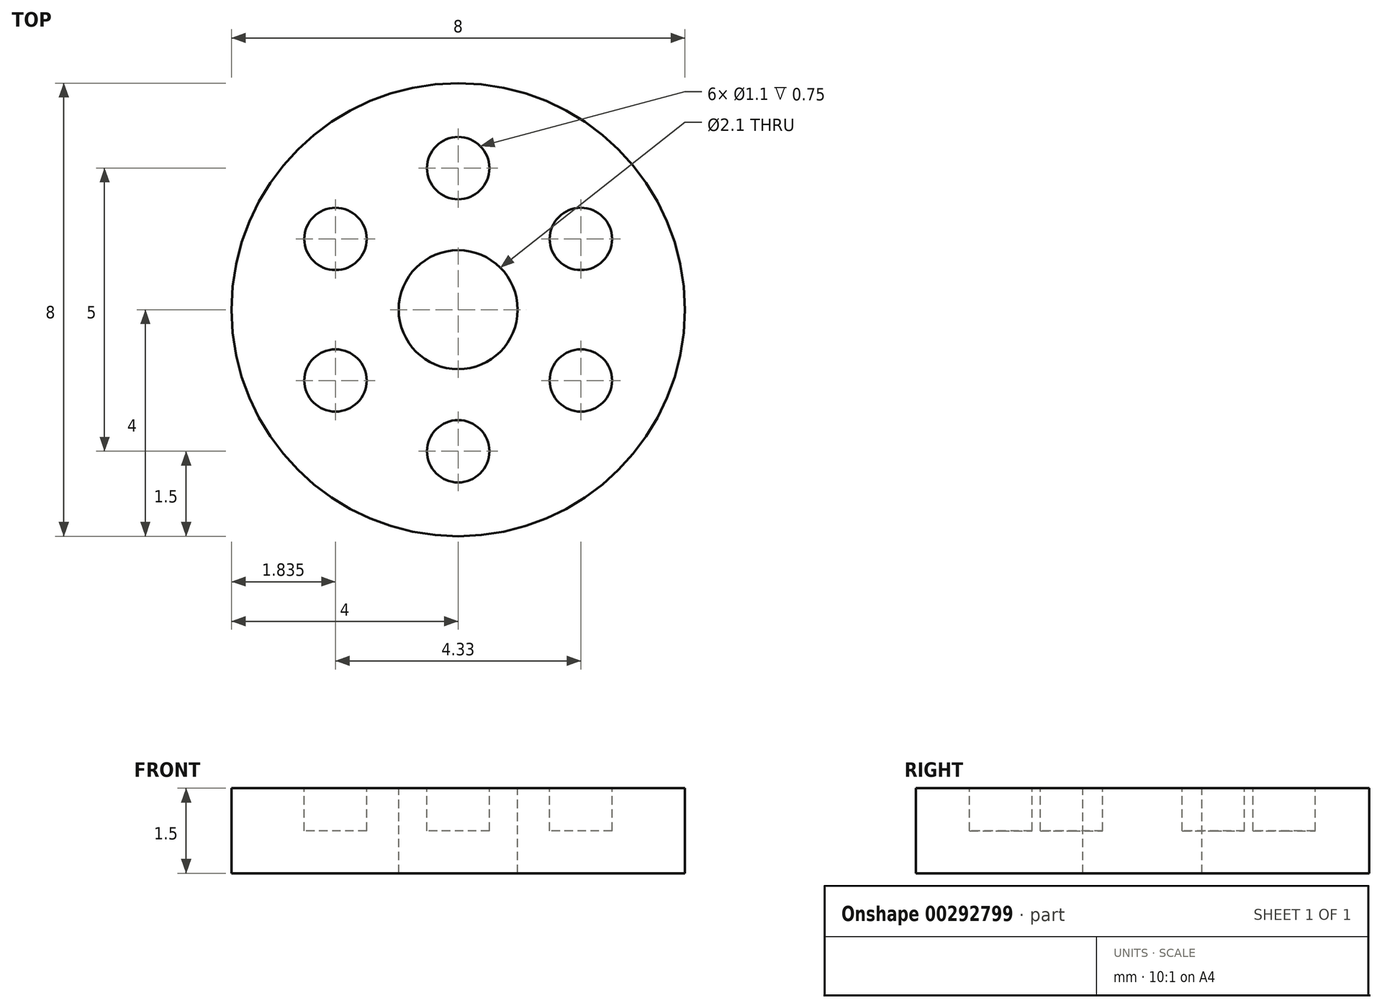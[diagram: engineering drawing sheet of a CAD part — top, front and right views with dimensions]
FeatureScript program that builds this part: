
annotation { "Feature Type Name" : "Feature", "Feature Type Description" : "" }
export const myFeature = defineFeature(function(context is Context, id is Id, definition is map)
    precondition{}
    {
        {
            var Q0;
            Q0=qCreatedBy(makeId("Top.planeOp"),FACE);
            var sketch = newSketch(context, id + "F0", { "sketchPlane" : qUnion([Q0])});
            skCircle(sketch, "E0", {"center": v(0, 0) * mm, "radius": 4 * mm});
            skSolve(sketch);
        }
        {
            var Q0;
            Q0 = qSketchRegion(id + "F0", true);
            extrude(context, id + "F1", {"entities" : qUnion([Q0]), "depth" : 1.5 * mm});
        }
        {
            var Q0;
            Q0=makeQuery(id+"F1.opExtrude","CAP_FACE",FACE,{"disambiguationData":[OSD([sQuery(id+"F0.wireOp",EDGE,"E0")])],"isStart":false});
            var sketch = newSketch(context, id + "F2", { "sketchPlane" : qUnion([Q0])});
            skCircle(sketch, "E1", {"center": v(0, 2.5) * mm, "radius": 0.55 * mm});
            skCircle(sketch, "E2.1.0", {"center": v(-2.17, 1.25) * mm, "radius": 0.55 * mm});
            skCircle(sketch, "E2.2.0", {"center": v(-2.17, -1.25) * mm, "radius": 0.55 * mm});
            skPoint(sketch, "E2.center", {"position": v(0, 0) * mm});
            skLineSegment(sketch, "E3", {"start": v(0, 0) * mm, "end": v(0, 2.5) * mm});
            skCircle(sketch, "E4.1.3.0", {"center": v(0, -2.5) * mm, "radius": 0.55 * mm});
            skCircle(sketch, "E4.1.4.0", {"center": v(2.17, -1.25) * mm, "radius": 0.55 * mm});
            skCircle(sketch, "E4.1.5.0", {"center": v(2.17, 1.25) * mm, "radius": 0.55 * mm});
            skSolve(sketch);
        }
        {
            var Q0;
            Q0=makeQuery(id+"F2.imprint","IMPRINT",FACE,{"disambiguationData":[TD([[makeQuery(id+"F2.imprint","IMPRINT",EDGE,{"derivedFrom":sQuery(id+"F2.wireOp",EDGE,"E1")}),1.0]])]});
            var Q1;
            Q1=makeQuery(id+"F2.imprint","IMPRINT",FACE,{"disambiguationData":[TD([[makeQuery(id+"F2.imprint","IMPRINT",EDGE,{"derivedFrom":sQuery(id+"F2.wireOp",EDGE,"E2.1.0")}),1.0]])]});
            var Q2;
            Q2=makeQuery(id+"F2.imprint","IMPRINT",FACE,{"disambiguationData":[TD([[makeQuery(id+"F2.imprint","IMPRINT",EDGE,{"derivedFrom":sQuery(id+"F2.wireOp",EDGE,"E2.2.0")}),1.0]])]});
            var Q3;
            Q3=makeQuery(id+"F2.imprint","IMPRINT",FACE,{"disambiguationData":[TD([[makeQuery(id+"F2.imprint","IMPRINT",EDGE,{"derivedFrom":sQuery(id+"F2.wireOp",EDGE,"E4.1.5.0")}),1.0]])]});
            var Q4;
            Q4=makeQuery(id+"F2.imprint","IMPRINT",FACE,{"disambiguationData":[TD([[makeQuery(id+"F2.imprint","IMPRINT",EDGE,{"derivedFrom":sQuery(id+"F2.wireOp",EDGE,"E4.1.4.0")}),1.0]])]});
            var Q5;
            Q5=makeQuery(id+"F2.imprint","IMPRINT",FACE,{"disambiguationData":[TD([[makeQuery(id+"F2.imprint","IMPRINT",EDGE,{"derivedFrom":sQuery(id+"F2.wireOp",EDGE,"E4.1.3.0")}),1.0]])]});
            extrude(context, id + "F3", {"entities" : qUnion([Q0, Q1, Q2, Q3, Q4, Q5]), "operationType" : NewBodyOperationType.REMOVE, "oppositeDirection" : true, "depth" : 0.75 * mm});
        }
        {
            var Q0;
            Q0=makeQuery(id+"F1.opExtrude","CAP_FACE",FACE,{"disambiguationData":[OSD([sQuery(id+"F0.wireOp",EDGE,"E0")])],"isStart":false});
            var sketch = newSketch(context, id + "F4", { "sketchPlane" : qUnion([Q0])});
            skCircle(sketch, "E5", {"center": v(0, 0) * mm, "radius": 1.05 * mm});
            skSolve(sketch);
        }
        {
            var Q0;
            Q0=makeQuery(id+"F4.imprint","IMPRINT",FACE,{"disambiguationData":[TD([[makeQuery(id+"F4.imprint","IMPRINT",EDGE,{"derivedFrom":sQuery(id+"F4.wireOp",EDGE,"E5")}),1.0]])]});
            extrude(context, id + "F5", {"entities" : qUnion([Q0]), "operationType" : NewBodyOperationType.REMOVE, "oppositeDirection" : true, "depth" : 25 * mm});
        }
    });
